FCSTD DOCUMENT  (FreeCAD 1.1R20260108 (Git shallow))
Label: Parts
License: All rights reserved
LicenseURL: http://en.wikipedia.org/wiki/All_rights_reserved
objects: Sketcher::SketchObject×1
note: 2 computed .brp shape members not serialized (recipe doc carries the construction recipe); baked Part::Feature solids carry a one-line shape summary decoded from their .brp

FEATURE [Sketcher::SketchObject] Sketch  label="MasterSketch"
  ArcFitTolerance = 1e-06
  ExternalTypes = [0]
  FullyConstrained = true
  MakeInternals = false
  sketch-geometry (19):
    g0: ArcOfCircle CenterX=5e-16 CenterY=55 CenterZ=0 NormalX=0 NormalY=0 NormalZ=1 AngleXU=0 Radius=10 StartAngle=3e-16 EndAngle=3.14159
    g1: ArcOfCircle CenterX=-5e-16 CenterY=-55 CenterZ=0 NormalX=0 NormalY=0 NormalZ=1 AngleXU=0 Radius=10 StartAngle=3.14159 EndAngle=6.28319
    g2: LineSegment StartX=10 StartY=55 StartZ=0 EndX=10 EndY=-55 EndZ=0
    g3: LineSegment StartX=-10 StartY=55 StartZ=0 EndX=-10 EndY=-55 EndZ=0
    g4: Circle CenterX=5e-16 CenterY=55 CenterZ=0 NormalX=0 NormalY=0 NormalZ=1 AngleXU=0 Radius=3.5
    g5: Circle CenterX=-5e-16 CenterY=-55 CenterZ=0 NormalX=0 NormalY=0 NormalZ=1 AngleXU=0 Radius=3.5
    g6: LineSegment StartX=-30 StartY=80 StartZ=0 EndX=-30 EndY=20 EndZ=0
    g7: LineSegment StartX=-30 StartY=20 StartZ=0 EndX=30 EndY=20 EndZ=0
    g8: LineSegment StartX=30 StartY=20 StartZ=0 EndX=30 EndY=80 EndZ=0
    g9: LineSegment StartX=30 StartY=80 StartZ=0 EndX=-30 EndY=80 EndZ=0
    g10: ArcOfCircle CenterX=0 CenterY=-25 CenterZ=0 NormalX=0 NormalY=0 NormalZ=1 AngleXU=0 Radius=25 StartAngle=6.01325 EndAngle=9.69471
    g11: ArcOfCircle CenterX=-5e-16 CenterY=-55 CenterZ=0 NormalX=0 NormalY=0 NormalZ=1 AngleXU=0 Radius=17 StartAngle=3.41153 EndAngle=6.01325
    g12: LineSegment StartX=-24.0947 StartY=-31.6667 StartZ=0 EndX=-16.3844 EndY=-59.5333 EndZ=0
    g13: LineSegment StartX=16.3844 StartY=-59.5333 StartZ=0 EndX=24.0947 EndY=-31.6667 EndZ=0
    g14: ArcOfCircle CenterX=0 CenterY=-40 CenterZ=0 NormalX=0 NormalY=0 NormalZ=1 AngleXU=0 Radius=10 StartAngle=-5.77e-14 EndAngle=3.14159
    g15: LineSegment StartX=10 StartY=-40 StartZ=0 EndX=10 EndY=-100 EndZ=0
    g16: LineSegment StartX=-10 StartY=-40 StartZ=0 EndX=-10 EndY=-100 EndZ=0
    g17: Circle CenterX=0 CenterY=-40 CenterZ=0 NormalX=0 NormalY=0 NormalZ=1 AngleXU=0 Radius=3.5
    g18: LineSegment StartX=-10 StartY=-100 StartZ=0 EndX=10 EndY=-100 EndZ=0
  constraints (46):
    c: Tangent(g0,g2) = 1.5708
    c: Tangent(g0,g3) = -1.5708
    c: Tangent(g1,g2) = 1.5708
    c: Tangent(g1,g3) = -1.5708
    c: Equal(g0,g1)
    c: Vertical(g2)
    c: DistanceY(g1,g0) = 110
    c: Coincident(g4,g0)
    c: Coincident(g5,g1)
    c: Equal(g5,g4)
    c: Diameter(g4) = 7
    c: Radius(g0) = 10
    c: Symmetric(g0,g1,g-1)
    c: Coincident(g6,g7)
    c: Coincident(g7,g8)
    c: Coincident(g8,g9)
    c: Coincident(g9,g6)
    c: Vertical(g6)
    c: Vertical(g8)
    c: Horizontal(g7)
    c: Distance(g6,g8) = 60
    c: Equal(g6,g9)
    c: Symmetric(g6,g8,g-2)
    c: DistanceY(g-1,g6) = 20
    c: PointOnObject(g10,g-2)
    c: Radius(g10) = 25
    c: Radius(g11) = 17
    c: Coincident(g11,g1)
    c: Tangent(g13,g11) = -1.5708
    c: Tangent(g13,g10) = -1.5708
    c: Tangent(g12,g11) = -1.5708
    c: Tangent(g12,g10) = -1.5708
    c: DistanceY(g1,g10) = 30
    c: Tangent(g14,g15) = 1.5708
    c: Tangent(g14,g16) = -1.5708
    c: Vertical(g15)
    c: Equal(g14,g1)
    c: Coincident(g17,g14)
    c: Equal(g17,g5)
    c: Coincident(g18,g16)
    c: Coincident(g18,g15)
    c: Horizontal(g18)
    c: Vertical(g16)
    c: DistanceY(g16,g16) = 60
    c: PointOnObject(g14,g-2)
    c: DistanceY(g14,g10) = 15
